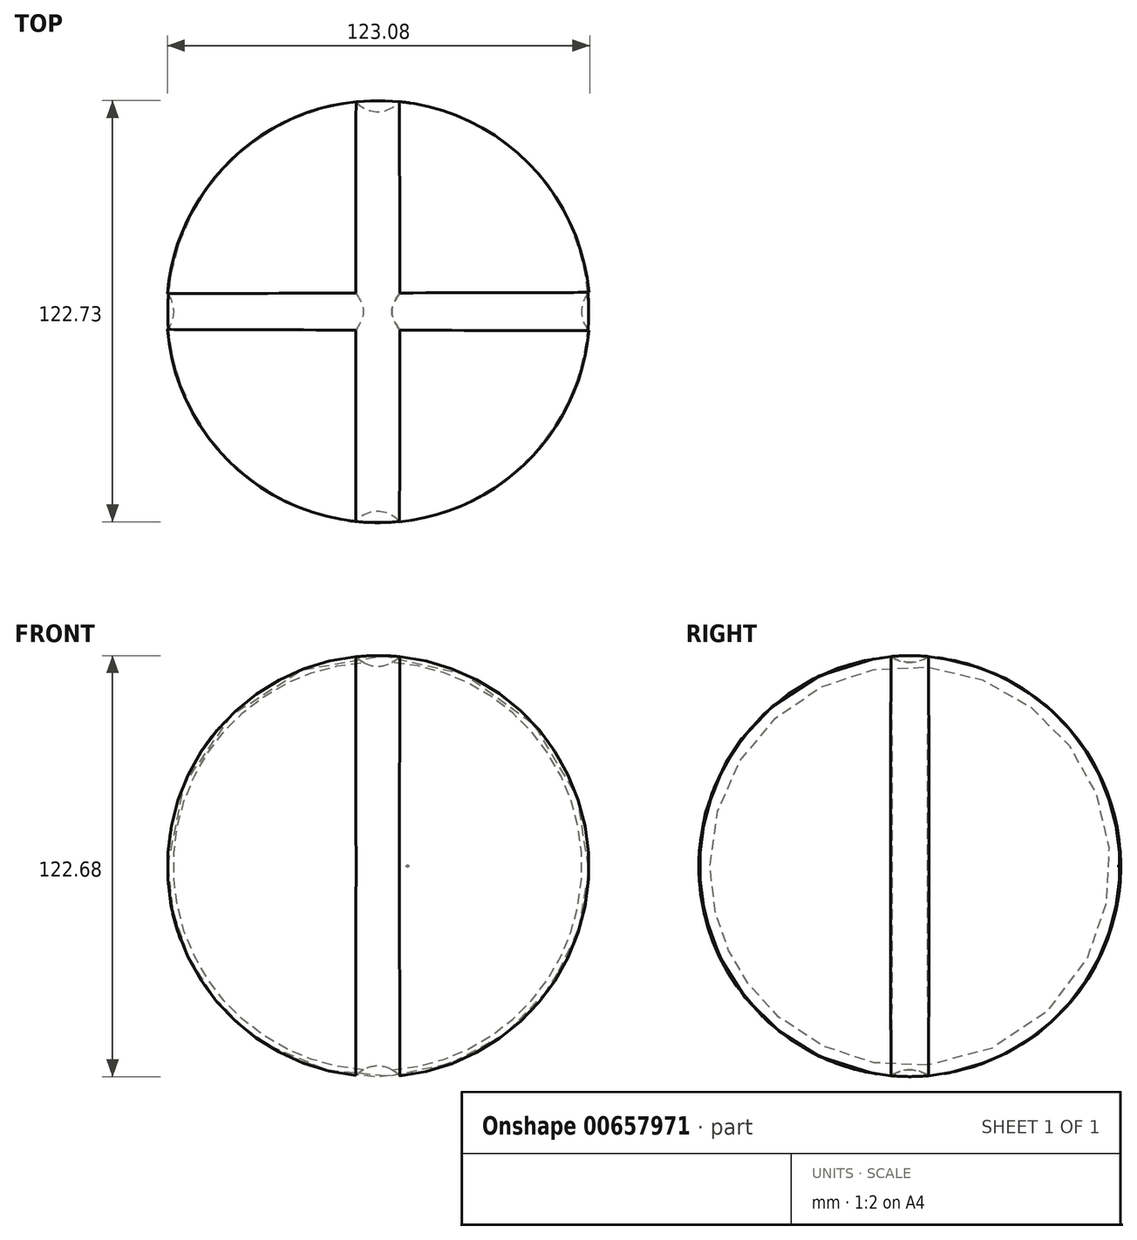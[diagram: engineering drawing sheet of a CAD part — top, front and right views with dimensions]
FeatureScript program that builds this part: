
annotation { "Feature Type Name" : "Feature", "Feature Type Description" : "" }
export const myFeature = defineFeature(function(context is Context, id is Id, definition is map)
    precondition{}
    {
        {
            var Q0;
            Q0=qCreatedBy(makeId("Top.planeOp"),FACE);
            var sketch = newSketch(context, id + "F0", { "sketchPlane" : qUnion([Q0])});
            skArc(sketch, "E0", {"start": v(8.68, 60.87) * mm, "mid": v(-60.9, 8.52) * mm, "end": v(-8.36, -60.92) * mm});
            skLineSegment(sketch, "E1", {"start": v(-8.36, -60.92) * mm, "end": v(8.68, 60.87) * mm});
            skSolve(sketch);
        }
        {
            var Q0;
            Q0=makeQuery(id+"F0.imprint","IMPRINT",FACE,{"disambiguationData":[TD([[makeQuery(id+"F0.imprint","IMPRINT",EDGE,{"derivedFrom":sQuery(id+"F0.wireOp",EDGE,"E0")}),1.0]])]});
            var Q1;
            Q1=sQuery(id+"F0.wireOp",EDGE,"E1");
            revolve(context, id + "F1", {"entities" : qUnion([Q0]), "axis" : qUnion([Q1]), "revolveType" : RevolveType.FULL});
        }
        {
            var Q0;
            Q0=qCreatedBy(makeId("Front.planeOp"),FACE);
            var sketch = newSketch(context, id + "F2", { "sketchPlane" : qUnion([Q0])});
            skCircle(sketch, "E2", {"center": v(0, 0) * mm, "radius": 68.36 * mm});
            skSolve(sketch);
        }
        {
            var Q0;
            Q0=qCreatedBy(makeId("Top.planeOp"),FACE);
            var sketch = newSketch(context, id + "F3", { "sketchPlane" : qUnion([Q0])});
            skCircle(sketch, "E3", {"center": v(68.12, 0) * mm, "radius": 8.62 * mm});
            skSolve(sketch);
        }
        {
            var Q0;
            Q0=makeQuery(id+"F3.imprint","IMPRINT",FACE,{"disambiguationData":[TD([[makeQuery(id+"F3.imprint","IMPRINT",EDGE,{"derivedFrom":sQuery(id+"F3.wireOp",EDGE,"E3")}),1.0]])]});
            var Q1;
            Q1=sQuery(id+"F2.wireOp",EDGE,"E2");
            revolve(context, id + "F4", {"operationType" : NewBodyOperationType.REMOVE, "entities" : qUnion([Q0]), "axis" : qUnion([Q1]), "revolveType" : RevolveType.FULL, "oppositeDirection" : true});
        }
        {
            var Q0;
            Q0=qCreatedBy(makeId("Right.planeOp"),FACE);
            var sketch = newSketch(context, id + "F5", { "sketchPlane" : qUnion([Q0])});
            skCircle(sketch, "E4", {"center": v(0, 0) * mm, "radius": 65.63 * mm});
            skSolve(sketch);
        }
        {
            var Q0;
            Q0=qCreatedBy(makeId("Front.planeOp"),FACE);
            var sketch = newSketch(context, id + "F6", { "sketchPlane" : qUnion([Q0])});
            skCircle(sketch, "E5", {"center": v(0, 66.46) * mm, "radius": 8.23 * mm});
            skSolve(sketch);
        }
        {
            var Q0;
            Q0=makeQuery(id+"F6.imprint","IMPRINT",FACE,{"disambiguationData":[TD([[makeQuery(id+"F6.imprint","IMPRINT",EDGE,{"derivedFrom":sQuery(id+"F6.wireOp",EDGE,"E5")}),1.0]])]});
            var Q1;
            Q1=sQuery(id+"F5.wireOp",EDGE,"E4");
            revolve(context, id + "F7", {"operationType" : NewBodyOperationType.REMOVE, "entities" : qUnion([Q0]), "axis" : qUnion([Q1]), "revolveType" : RevolveType.FULL, "oppositeDirection" : true});
        }
    });
